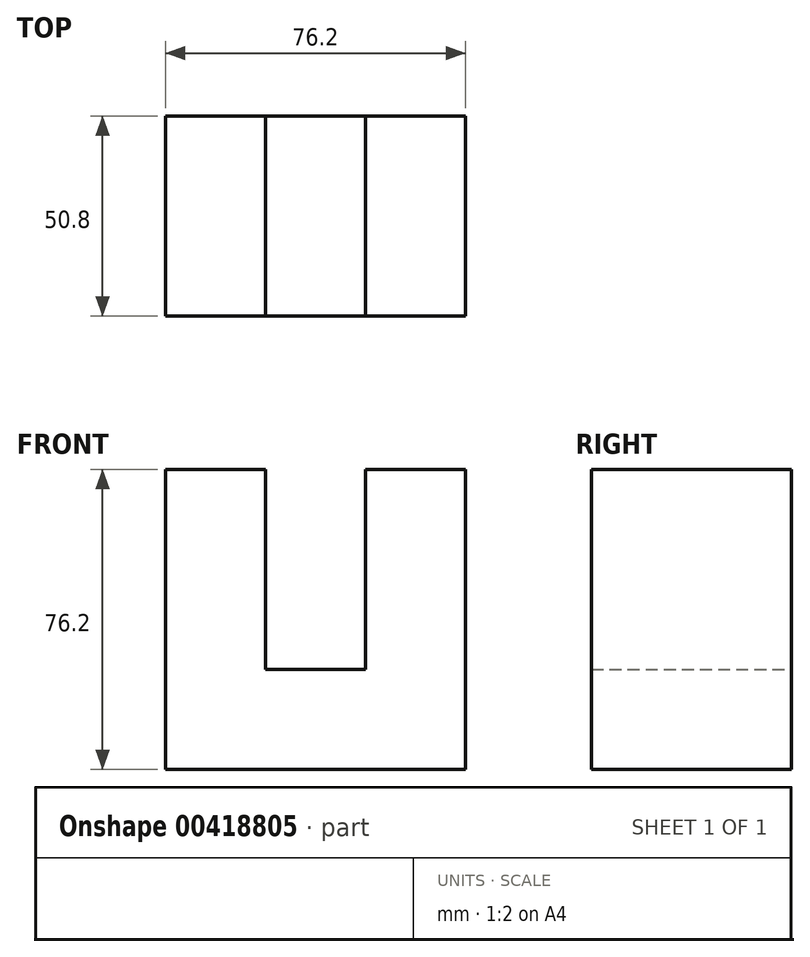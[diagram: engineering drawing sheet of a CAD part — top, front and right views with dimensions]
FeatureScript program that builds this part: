
annotation { "Feature Type Name" : "Feature", "Feature Type Description" : "" }
export const myFeature = defineFeature(function(context is Context, id is Id, definition is map)
    precondition{}
    {
        {
            var Q0;
            Q0=qCreatedBy(makeId("Front.planeOp"),FACE);
            var sketch = newSketch(context, id + "F0", { "sketchPlane" : qUnion([Q0])});
            skLineSegment(sketch, "E0", {"start": v(0, 0) * mm, "end": v(-76.2, 0) * mm});
            skLineSegment(sketch, "E1", {"start": v(-76.2, 0) * mm, "end": v(-76.2, 76.2) * mm});
            skLineSegment(sketch, "E2", {"start": v(-76.2, 76.2) * mm, "end": v(-50.8, 76.2) * mm});
            skLineSegment(sketch, "E3", {"start": v(-50.8, 76.2) * mm, "end": v(-50.8, 25.4) * mm});
            skLineSegment(sketch, "E4", {"start": v(-50.8, 25.4) * mm, "end": v(-25.4, 25.4) * mm});
            skLineSegment(sketch, "E5", {"start": v(-25.4, 25.4) * mm, "end": v(-25.4, 76.2) * mm});
            skLineSegment(sketch, "E6", {"start": v(-25.4, 76.2) * mm, "end": v(0, 76.2) * mm});
            skLineSegment(sketch, "E7", {"start": v(0, 76.2) * mm, "end": v(0, 0) * mm});
            skSolve(sketch);
        }
        {
            var Q0;
            Q0=makeQuery(id+"F0.imprint","IMPRINT",FACE,{"disambiguationData":[TD([[makeQuery(id+"F0.imprint","IMPRINT",EDGE,{"derivedFrom":sQuery(id+"F0.wireOp",EDGE,"E0")}),-1.0]])]});
            extrude(context, id + "F1", {"entities" : qUnion([Q0]), "depth" : 50.8 * mm});
        }
    });
